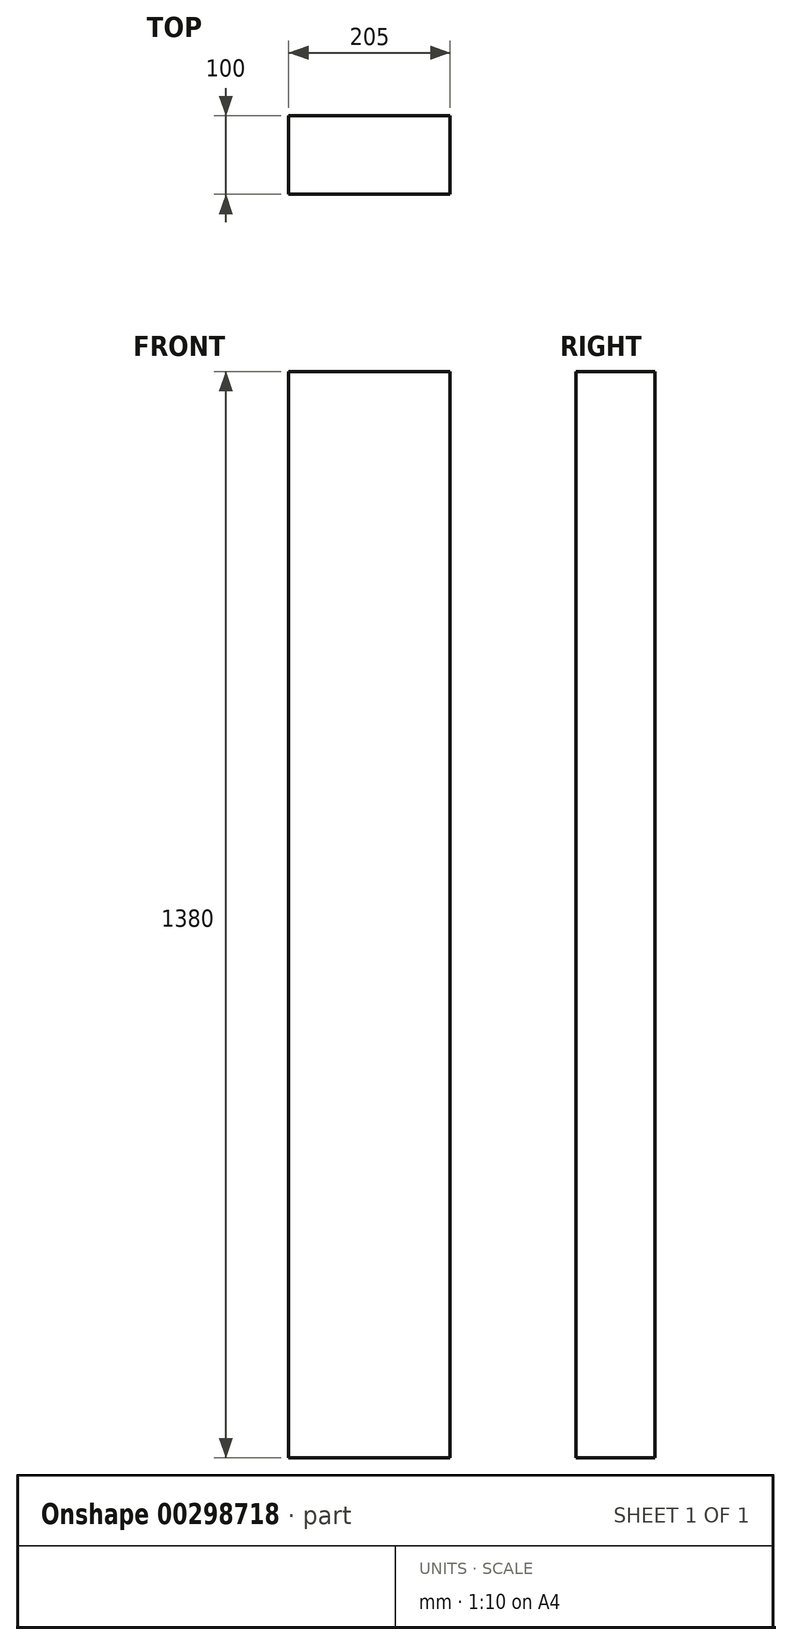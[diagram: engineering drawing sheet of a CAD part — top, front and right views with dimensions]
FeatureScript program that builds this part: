
annotation { "Feature Type Name" : "Feature", "Feature Type Description" : "" }
export const myFeature = defineFeature(function(context is Context, id is Id, definition is map)
    precondition{}
    {
        {
            var Q0;
            Q0=qCreatedBy(makeId("Front.planeOp"),FACE);
            var sketch = newSketch(context, id + "F0", { "sketchPlane" : qUnion([Q0])});
            skLineSegment(sketch, "E0.bottom", {"start": v(0, 0) * mm, "end": v(205, 0) * mm});
            skLineSegment(sketch, "E0.top", {"start": v(0, 1380) * mm, "end": v(205, 1380) * mm});
            skLineSegment(sketch, "E0.left", {"start": v(0, 0) * mm, "end": v(0, 1380) * mm});
            skLineSegment(sketch, "E0.right", {"start": v(205, 0) * mm, "end": v(205, 1380) * mm});
            skSolve(sketch);
        }
        {
            var Q0;
            Q0=makeQuery(id+"F0.imprint","IMPRINT",FACE,{"disambiguationData":[TD([[makeQuery(id+"F0.imprint","IMPRINT",EDGE,{"derivedFrom":sQuery(id+"F0.wireOp",EDGE,"E0.bottom")}),1.0]])]});
            extrude(context, id + "F1", {"entities" : qUnion([Q0]), "depth" : 100 * mm});
        }
    });
